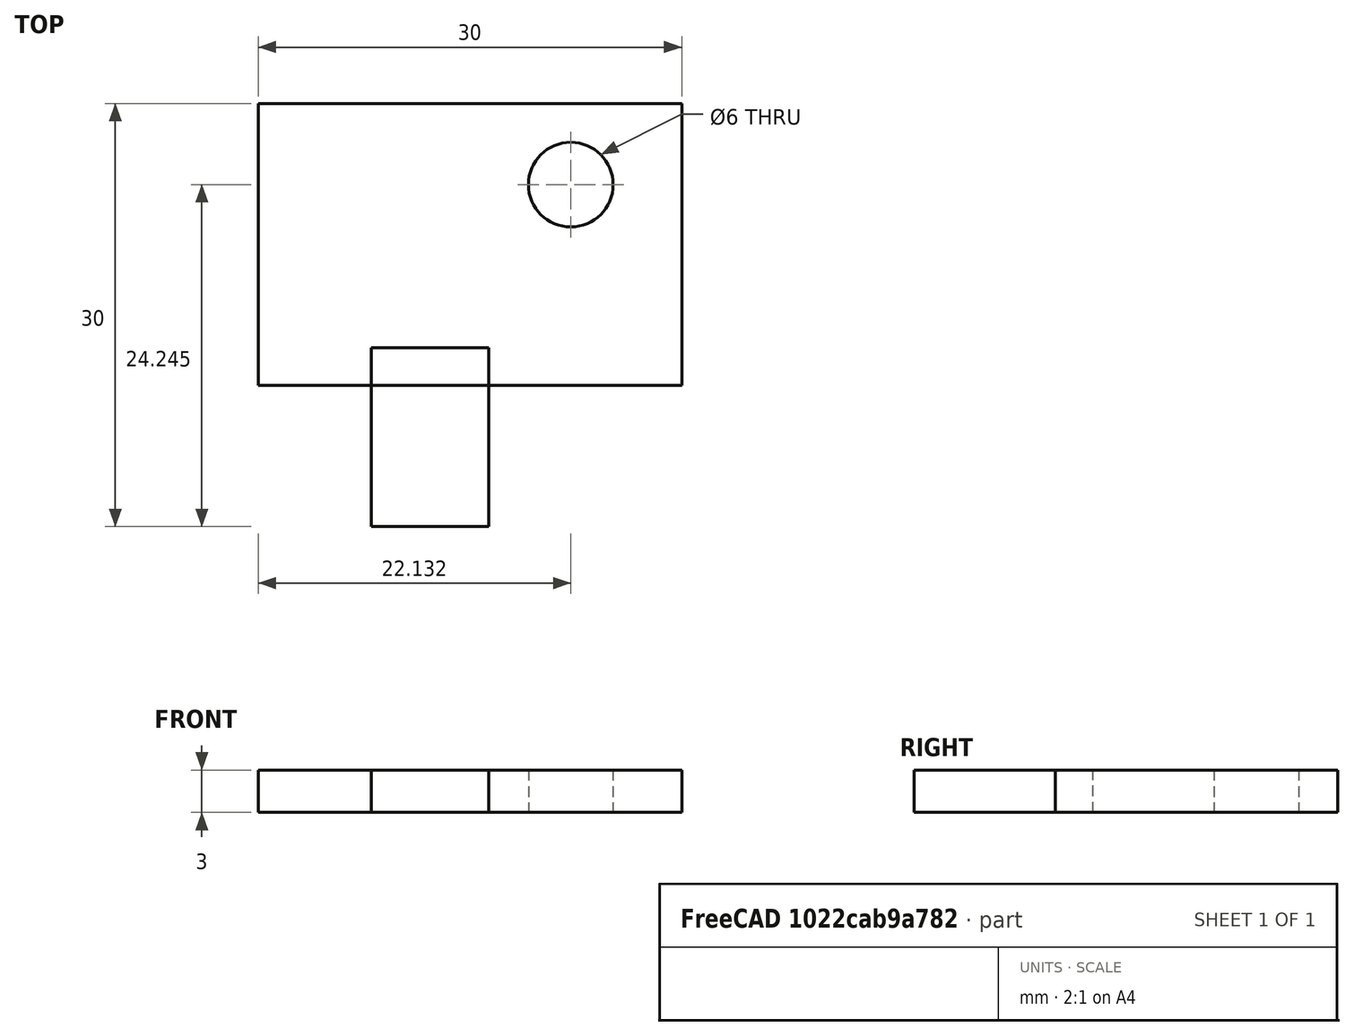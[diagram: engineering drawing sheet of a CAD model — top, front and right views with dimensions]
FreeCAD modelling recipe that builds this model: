
FCSTD DOCUMENT  (FreeCAD 0.18R16131 (Git))
Label: Patch Antenna 1
License: All rights reserved
LicenseURL: http://en.wikipedia.org/wiki/All_rights_reserved
objects: Part::Part2DObjectPython×4, Part::Extrusion×4, Sketcher::SketchObject×2, Fem::ConstraintTemperature×2, Fem::FemMeshObjectPython×2, Fem::FemSolverObjectPython×1, Part::Fuse×1, PartDesign::FeatureBase×1, PartDesign::Hole×1, PartDesign::Body×1, Fem::ConstraintInitialTemperature×1, App::MaterialObjectPython×1, Fem::ConstraintFixed×1, Fem::ConstraintForce×1, Fem::FemResultObjectPython×1, Fem::FemAnalysis×1, Fem::FemPostPipeline×1
note: 15 computed .brp shape members not serialized (recipe doc carries the construction recipe); baked Part::Feature solids carry a one-line shape summary decoded from their .brp

FEATURE [Part::Part2DObjectPython] Rectangle  # Draft 2D object (typed FeaturePython)
  ChamferSize = 0
  Columns = 1
  FilletRadius = 0
  Height = 12.6692
  Length = 8.31771
  MakeFace = false
  Placement = pos=(-2,-10,0) rot=(0,0,1;0rad)
  Rows = 1
FEATURE [Part::Part2DObjectPython] Rectangle001  # Draft 2D object (typed FeaturePython)
  ChamferSize = 0
  Columns = 1
  FilletRadius = 0
  Height = 20
  Length = 30
  MakeFace = false
  Placement = pos=(-10,-1e-15,0) rot=(0,0,1;0rad)
  Rows = 1
FEATURE [Part::Extrusion] Extrude
  Base = -> Rectangle
  Dir = (0,0,1)
  DirMode = 2
  FaceMakerClass = Part::FaceMakerBullseye
  LengthFwd = 3
  LengthRev = 0
  Solid = true
  Symmetric = false
FEATURE [Part::Extrusion] Extrude001
  Base = -> Rectangle001
  Dir = (0,0,1)
  DirMode = 2
  FaceMakerClass = Part::FaceMakerBullseye
  LengthFwd = 3
  LengthRev = 0
  Solid = true
  Symmetric = false
FEATURE [Fem::FemSolverObjectPython] CalculiXccxTools  # FEM object (typed FeaturePython)
  AnalysisType = 2
  BeamShellResultOutput3D = false
  EigenmodeHighLimit = 1000000
  EigenmodeLowLimit = 0
  EigenmodesCount = 10
  GeometricalNonlinearity = 0
  IterationsControlParameterCutb = 0.25,0.5,0.75,0.85,,,1.5,
  IterationsControlParameterIter = 4,8,9,200,10,400,,200,,
  IterationsControlParameterTimeUse = false
  IterationsThermoMechMaximum = 2000
  IterationsUserDefinedIncrementations = false
  IterationsUserDefinedTimeStepLength = false
  MaterialNonlinearity = 0
  MatrixSolverType = 0
  SplitInputWriter = false
  ThermoMechSteadyState = true
  TimeEnd = 1
  TimeInitialStep = 1
FEATURE [Sketcher::SketchObject] Sketch
  MapMode = 5
  Placement = pos=(0,0,3) rot=(0,0,1;0rad)
  sketch-geometry (1):
    g0: Circle CenterX=12.1322 CenterY=14.2453 CenterZ=0 NormalX=0 NormalY=0 NormalZ=1 AngleXU=0 Radius=2.45211
FEATURE [Part::Part2DObjectPython] Rectangle002  # Draft 2D object (typed FeaturePython)
  ChamferSize = 0
  Columns = 1
  FilletRadius = 0
  Height = 20
  Length = 30
  MakeFace = false
  Placement = pos=(-10,-1e-15,0) rot=(0,0,1;0rad)
  Rows = 1
FEATURE [Part::Extrusion] Extrude002
  Base = -> Rectangle002
  Dir = (0,0,1)
  DirMode = 2
  FaceMakerClass = Part::FaceMakerBullseye
  LengthFwd = 3
  LengthRev = 0
  Solid = true
  Symmetric = false
FEATURE [Part::Part2DObjectPython] Rectangle003  # Draft 2D object (typed FeaturePython)
  ChamferSize = 0
  Columns = 1
  FilletRadius = 0
  Height = 12.6692
  Length = 8.31771
  MakeFace = false
  Placement = pos=(-2,-10,0) rot=(0,0,1;0rad)
  Rows = 1
FEATURE [Part::Extrusion] Extrude003
  Base = -> Rectangle003
  Dir = (0,0,1)
  DirMode = 2
  FaceMakerClass = Part::FaceMakerBullseye
  LengthFwd = 3
  LengthRev = 0
  Solid = true
  Symmetric = false
FEATURE [Part::Fuse] Fusion001
  Base = -> Extrude003
  Tool = -> Extrude002
FEATURE [Sketcher::SketchObject] CopySketch
  Placement = pos=(0,0,3) rot=(0,0,1;0rad)
  sketch-geometry (1):
    g0: Circle CenterX=12.1322 CenterY=14.2453 CenterZ=0 NormalX=0 NormalY=0 NormalZ=1 AngleXU=0 Radius=2.45211
FEATURE [PartDesign::FeatureBase] BaseFeature
  BaseFeature = -> Fusion001
FEATURE [PartDesign::Hole] Hole
  BaseFeature = -> BaseFeature
  Depth = 25
  DepthType = 0
  Diameter = 6
  DrillPoint = 1
  DrillPointAngle = 118
  HoleCutCountersinkAngle = 90
  HoleCutDepth = 0
  HoleCutDiameter = 0
  HoleCutType = 0
  ModelActualThread = false
  Profile = -> Sketch
  Tapered = false
  TaperedAngle = 90
  ThreadAngle = 0
  ThreadClass = 0
  ThreadCutOffInner = 0
  ThreadCutOffOuter = 0
  ThreadDirection = 0
  ThreadFit = 0
  ThreadPitch = 0
  ThreadSize = 0
  ThreadType = 0
  Threaded = false
FEATURE [PartDesign::Body] Body
  BaseFeature = -> Fusion001
  Group = -> [BaseFeature,Sketch,Hole]
  Origin = -> Origin
  Tip = -> Hole
FEATURE [Fem::ConstraintInitialTemperature] FemConstraintInitialTemperature
  NormalDirection = (0,0,1)
  initialTemperature = 300
FEATURE [Fem::ConstraintTemperature] FemConstraintTemperature
  CFlux = 0
  ConstraintType = 1
  NormalDirection = (1,-1e-16,0)
  Normals = (9) [(-1,0,0),(1,-1.22465e-16,0),(-1,2.44929e-16,0),(-1,0,0),(1,-1.22465e-16,0),(-1,2.44929e-16,0),(-1,0,0),(1,-1.22465e-16,0),(-1,2.44929e-16,0)]
  Points = (9) [(15.1322,14.2453,3),(9.13221,14.2453,3),(15.1322,14.2453,3),(15.1322,14.2453,1.5),(9.13221,14.2453,1.5),(15.1322,14.2453,1.5),(15.1322,14.2453,0),+2 more]
  References = -> [Hole]
  Temperature = 1000
FEATURE [Fem::ConstraintTemperature] FemConstraintTemperature001
  CFlux = 0
  ConstraintType = 1
  NormalDirection = (0,-1,0)
  Normals = (9) [(3e-17,-1,0),(3e-17,-1,0),(3e-17,-1,0),(3e-17,-1,0),(3e-17,-1,0),(3e-17,-1,0),(3e-17,-1,0),(3e-17,-1,0),(3e-17,-1,0)]
  Points = (9) [(-2,-10,3),(2.15885,-10,3),(6.31771,-10,3),(-2,-10,1.5),(2.15885,-10,1.5),(6.31771,-10,1.5),(-2,-10,0),(2.15885,-10,0),(6.31771,-10,0)]
  References = -> [Hole]
  Temperature = 300
FEATURE [App::MaterialObjectPython] SolidMaterial001  label="glass generic"  # material (typed FeaturePython)
  Category = 0
  Material = Density=2700 kg/m^3,Description=Precipitation-hardened, Nonferrous Aluminum alloy,Father=Metal,KindOfMaterial=Aluminium,KindOfMaterialDE=Aluminium,+8 more (map truncated)
  References = -> [Hole]
FEATURE [Fem::FemMeshObjectPython] FEMMeshGmsh  # FEM object (typed FeaturePython)
  Algorithm2D = 0
  Algorithm3D = 0
  CharacteristicLengthMax = 2
  CharacteristicLengthMin = 0.8
  CoherenceMesh = true
  ElementDimension = 0
  ElementOrder = 1
  GeometryTolerance = 1e-06
  GroupsOfNodes = false
  HighOrderOptimize = false
  OptimizeNetgen = false
  OptimizeStd = true
  Part = -> Hole
  RecombineAll = false
FEATURE [Fem::ConstraintFixed] FemConstraintFixed
  NormalDirection = (-1,0,0)
  Normals = (9) [(-1,-3e-17,0),(-1,-3e-17,0),(-1,-3e-17,0),(-1,-3e-17,0),(-1,-3e-17,0),(-1,-3e-17,0),(-1,-3e-17,0),(-1,-3e-17,0),(-1,-3e-17,0)]
  Points = (9) [(-10,20,3),(-10,10,3),(-10,0,3),(-10,20,1.5),(-10,10,1.5),(-10,0,1.5),(-10,20,0),(-10,10,0),(-10,0,0)]
  References = -> [Hole]
FEATURE [Fem::ConstraintForce] FemConstraintForce
  DirectionVector = (0,-1,0)
  Force = 1
  NormalDirection = (0,1,0)
  Points = (12) [(20,20,3),(10,20,3),(0,20,3),(-10,20,3),(20,20,1.5),(10,20,1.5),(0,20,1.5),(-10,20,1.5),(20,20,0),(10,20,0),(0,20,0),(-10,20,0)]
  References = -> [Fusion001]
  Reversed = true
  Scale = 2
FEATURE [Fem::FemMeshObjectPython] Result_mesh  # FEM object (typed FeaturePython)
FEATURE [Fem::FemResultObjectPython] CalculiX_thermomech_results  # FEM object (typed FeaturePython)
  DisplacementLengths = [2.24997e-05,2.24989e-05,2.78358e-05,2.78343e-05,1.0904e-05,1.09048e-05,2.05219e-05,2.05201e-05,0,0,3.89804e-05,3.89805e-05,8.78946e-06,1.92779e-05,8.78816e-06,1.92769e-05,0,4.01026e-05,3.33358e-05,0,4.01047e-05,3.3341e-05,2.24999e-05,+3988 more]
  DisplacementVectors = (4011) [(-2.0963e-05,-8.17234e-06,1.04708e-08),(-2.09625e-05,-8.17141e-06,1.14317e-08),(-2.0938e-05,-1.83421e-05,8.30341e-09),+4008 more]
  Eigenmode = 0
  EigenmodeFrequency = 0
  MaxShear = [4.40343e-05,3.8933e-05,4.41099e-05,3.93347e-05,0.0205721,0.0202648,0.0116613,0.0114788,0.0481163,0.0484813,0.000185398,0.000185072,0.0162691,0.00641839,0.0162748,0.00642029,0.0595459,0.00554511,0.0211515,0.0595152,0.00554756,0.0210864,+3989 more]
  Mesh = -> Result_mesh
  NodeNumbers = [1,2,3,4,5,6,7,8,9,10,11,12,13,14,15,16,17,18,19,20,21,22,23,24,25,26,27,28,29,30,31,32,33,34,35,36,37,38,39,40,41,42,43,44,45,46,47,48,49,50,51,52,53,54,55,56,57,58,59,60,61,62,63,64,65,66,67,68,69,+3942 more]
  PrincipalMax = [1.04863e-05,9.98079e-06,1.16666e-05,7.88667e-06,-0.000426909,-0.0003894,-0.000894377,-0.00086379,-0.0295691,-0.0303293,0.000324795,0.000320701,0.00115117,6.02552e-05,0.00115202,5.63582e-05,0.150474,-4.51553e-06,-0.000522471,0.150829,+3991 more]
  PrincipalMed = [3.06545e-06,9.02741e-06,8.01787e-06,5.09185e-06,-0.0037309,-0.00361945,-0.00301091,-0.00291046,-0.0390146,-0.0392788,-1.85728e-06,-2.74451e-06,8.04957e-05,-0.00072538,7.99317e-05,-0.000722803,0.0473605,-0.000188058,-0.00284208,0.0476393,+3991 more]
  PrincipalMin = [-7.75823e-05,-6.78852e-05,-7.65533e-05,-7.07828e-05,-0.041571,-0.0409191,-0.0242169,-0.0238214,-0.125802,-0.127292,-4.60017e-05,-4.94433e-05,-0.0313871,-0.0127765,-0.0313976,-0.0127842,0.031382,-0.0110947,-0.0428255,0.0317984,-0.0111031,+3990 more]
  ResultType = Fem::FemResultMechanical
  Stats = [-2.09634e-05,-2.19411e-06,1.25773e-05,-3.82807e-05,-1.65713e-05,0,-5.41104e-07,3.1815e-09,5.46771e-07,0,1.82837e-05,4.01047e-05,6.94098e-06,0.0222657,0.129722,-0.0360307,0.00931998,0.194544,-0.0494157,-0.000256342,0.0824828,-0.127328,+17 more]
  StrainVectors = (4011) [(-2.70675e-10,-4.10273e-10,3.65435e-10),(-2.93719e-10,-3.68015e-10,4.20891e-10),(-3.66019e-10,-4.06351e-10,4.92148e-10),+4008 more]
  StressValues = [8.46026e-05,7.73937e-05,8.64533e-05,7.731e-05,0.0395956,0.0390151,0.0223396,0.0220057,0.0918746,0.092812,0.000350814,0.000349145,0.0320163,0.0124625,0.032027,0.0124693,0.111961,0.0109996,0.0411923,0.111954,0.0110004,0.0411234,3.09369e-05,+3988 more]
  StressVectors = (4011) [(-2.99298e-05,-3.71721e-05,3.07138e-06),(-2.73654e-05,-3.12199e-05,9.70832e-06),(-3.30993e-05,-3.51917e-05,1.14222e-05),+4008 more]
  Temperature = [300,300,300,300,697.122,697.042,727.524,727.415,781.956,781.955,919.706,919.705,751.722,795.14,751.72,795.136,854.376,993.877,1000,854.376,993.878,1000,300,300,300,300,300,300,300,300,300,300,300,300,300,300,300,300,300,300,300,300,300,300,+3967 more]
  Time = 1
FEATURE [Fem::FemAnalysis] Analysis
  Group = -> [CalculiXccxTools,FemConstraintInitialTemperature,FemConstraintTemperature,FemConstraintTemperature001,SolidMaterial001,FEMMeshGmsh,FemConstraintFixed,FemConstraintForce,CalculiX_thermomech_results]
FEATURE [Fem::FemPostPipeline] Pipeline
  Mode = 0
